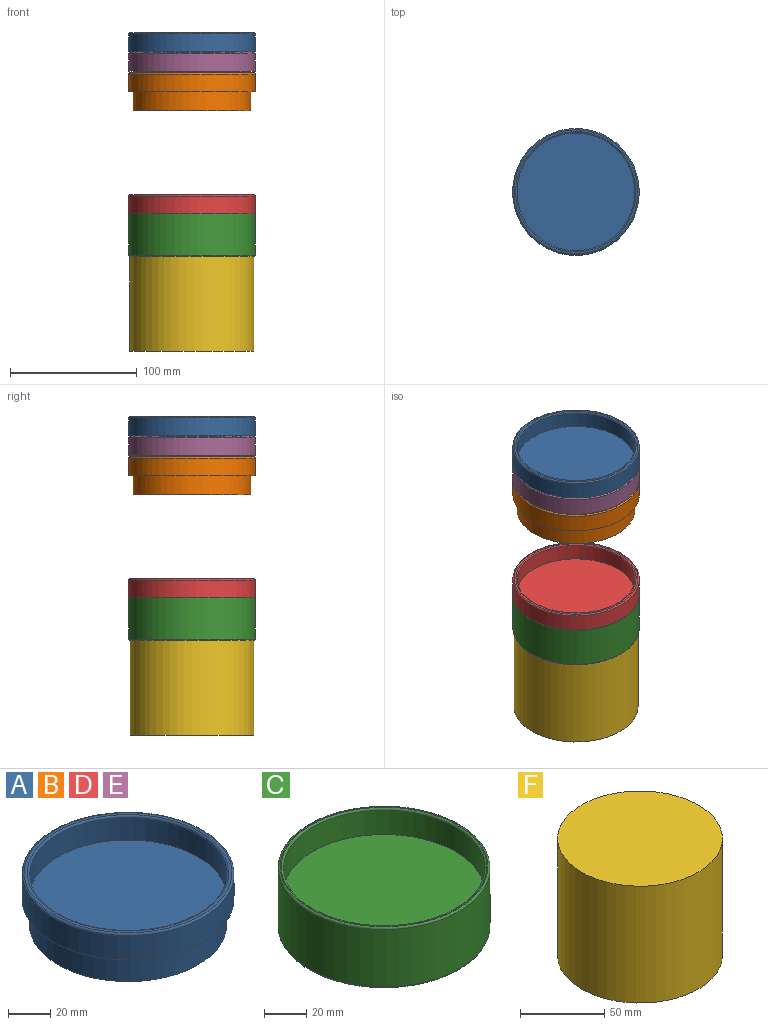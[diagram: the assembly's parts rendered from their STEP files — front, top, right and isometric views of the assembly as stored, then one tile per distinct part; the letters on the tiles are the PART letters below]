
ASSEMBLY  parts=6 mates=5
PART A: 9 faces, bbox 108.2x108.2x30 mm
  f0: cylinder r=46.5mm len=93mm, axis (0,0,-1), area 4382.5mm2, adj f1,f4
  f1: plane 93x93mm, normal (0,0,-1), area 6792.9mm2, adj f0
  f2: cylinder r=50mm len=100mm, axis (0,0,-1), area 4398.2mm2, adj f4,f8
  f3: plane 98x98mm, normal (0,0,1), area 454.7mm2, adj f7,f8
  f4: plane 100x100mm, normal (0,0,-1), area 1061.1mm2, adj f0,f2
  f5: cylinder r=46.5mm len=93mm, axis (0,0,1), area 3798.2mm2, adj f6,f7
  f6: plane 93x93mm, normal (0,0,1), area 6792.9mm2, adj f5
  f7: torus R=47.5mm, axis (0,0,1), area 462.5mm2, adj f3,f5
  f8: torus R=49mm, axis (0,0,1), area 489.9mm2, adj f2,f3
PART B: same geometry as A
PART C: 11 faces, bbox 108.2x108.2x35 mm
  f0: cylinder r=50mm len=100mm, axis (0,0,-1), area 10367.3mm2, adj f9,f10
  f1: plane 98x98mm, normal (0,0,-1), area 153.2mm2, adj f8,f10
  f2: plane 98x98mm, normal (0,0,1), area 153.2mm2, adj f7,f9
  f3: cylinder r=47.5mm len=95mm, axis (0,0,-1), area 2686.1mm2, adj f4,f8
  f4: plane 95x95mm, normal (0,0,-1), area 7088.2mm2, adj f3
  f5: cylinder r=47.5mm len=95mm, axis (0,0,1), area 4178.3mm2, adj f6,f7
  f6: plane 95x95mm, normal (0,0,1), area 7088.2mm2, adj f5
  f7: torus R=48.5mm, axis (0,0,1), area 472.4mm2, adj f2,f5
  f8: torus R=48.5mm, axis (0,0,1), area 472.4mm2, adj f1,f3
  f9: torus R=49mm, axis (0,0,1), area 489.9mm2, adj f0,f2
  f10: torus R=49mm, axis (0,0,1), area 489.9mm2, adj f0,f1
PART D: same geometry as A
PART E: same geometry as A
PART F: 3 faces, bbox 98x98x85 mm
  f0: cylinder r=49mm len=98mm, axis (0,0,1), area 26169.5mm2, adj f1,f2
  f1: plane 98x98mm, normal (0,0,-1), area 7543mm2, adj f0
  f2: plane 98x98mm, normal (0,0,1), area 7543mm2, adj f0
PLACE A t=(-132.97,-125.86,167.36)mm
PLACE B t=(-132.97,-125.86,135.6)mm
PLACE C t=(-132.97,-125.86,85.48)mm
PLACE D t=(-132.97,-125.86,39.24)mm
PLACE E t=(-132.97,-125.86,151.69)mm
PLACE F t=(-132.97,-125.86,85.48)mm
MATE slider A.f0 <-> E.f0  axis (0,0,-1) through (-132.97,-125.86,232.36)mm
MATE slider C.f5 <-> D.f0  axis (0,0,1) through (-132.97,-125.86,105.48)mm
MATE fastened C.f3 <-> F.f0  axis (0,0,-1) through (-132.97,-125.86,95.48)mm
MATE slider B.f0 <-> E.f0  axis (0,0,1) through (-132.97,-125.86,216.6)mm
MATE slider D.f0 <-> B.f0  axis (0,0,1) through (-132.97,-125.86,120.24)mm
